# Revit family: EVAN WBT
name_source: partatom
category: Оборудование
units: mm (PartAtom-declared; Revit-internal decimal feet)

## family parameters
Всегда вертикально = Да
Классификация = Нет
На основе рабочей плоскости = Нет
Общий = Нет
При загрузке вырезать с полостями = Нет
Размер круглого соединителя = Использовать диаметр
Тип детали = Нормальный
Точка расчета площади = Нет

## types (14) — shared parameters
ADSK_Классификация нагрузок = Прочее
ADSK_Количество фаз = 1
ADSK_Коэффициент мощности = 1
ADSK_Материал = Конструкционная сталь с эмалевым покрытием
ADSK_Напряжение = 0 В
ADSK_Номинальная мощность = 0 Вт
ADSK_Расход ГВ = 0.0 л/с
ADSK_Расход ХВ = 0.0 л/с
Dкороба = 20 мм
G1int = 30 мм
G2int = 24 мм
URL = https://www.evan.ru
База = Бойлер косвенного нагрева напольный
Высота 1 = 20 мм
Материал корпуса = Конструкционная сталь с эмалевым покрытием
Напряжение питания для ТЭНа, В = 0 В
Пластик прозрачный = Пластик_прозрачный
Пластик_красный = Пластик_красный
Пластик_синий = Пластик_синий
Пластмасса_черная = Пластмасса_черная
Серый = Серый
Стекло = Стекло
Частота тока для ТЭНа, Гц = 0 Гц
Электрическая мощность ТЭНа N, кВт2) = 0 Вт

## per-type parameters (varying)
| type | ADSK_Полная мощность | D2_colp | DN1 | DN2 | Dбойлера | G1ext | G2ext | H3 | H5 | H7 | Диаметр1 | Диаметр2 | Объем, л |
| EVAN WBT 100 л. с одним змеевиком | 17 кВт | 27 мм | 25 мм | 20 мм | 490 мм | 31 мм | 26 мм | 554 мм | 854 мм | 734 мм | 236 мм | 239 мм | 104 |
| EVAN WBT 160 л. с одним змеевиком | 24 кВт | 27 мм | 25 мм | 20 мм | 590 мм | 31 мм | 26 мм | 542 мм | 857 мм | 707 мм | 286 мм | 289 мм | 173 |
| EVAN WBT 200 л. с одним змеевиком | 27 кВт | 27 мм | 25 мм | 20 мм | 590 мм | 31 мм | 26 мм | 679 мм | 1074 мм | 864 мм | 286 мм | 289 мм | 208 |
| EVAN WBT 300 л. с одним змеевиком | 36 кВт | 33 мм | 25 мм | 25 мм | 590 мм | 31 мм | 31 мм | 738 мм | 1613 мм | 913 мм | 286 мм | 289 мм | 284 |
| EVAN WBT 400 л. с одним змеевиком | 43 кВт | 33 мм | 25 мм | 25 мм | 750 мм | 31 мм | 31 мм | 698 мм | 1143 мм | 893 мм | 366 мм | 369 мм | 409 |
| EVAN WBT 500 л. с одним змеевиком | 53 кВт | 33 мм | 25 мм | 25 мм | 750 мм | 31 мм | 31 мм | 761 мм | 1386 мм | 986 мм | 366 мм | 369 мм | 510 |
| EVAN WBT 800 л. с одним змеевиком | 69 кВт | 40 мм | 32 мм | 32 мм | 950 мм | 38 мм | 38 мм | 843 мм | 1368 мм | 1063 мм | 466 мм | 469 мм | 814 |
| EVAN WBT 1000 л. с одним змеевиком | 82 кВт | 40 мм | 32 мм | 32 мм | 950 мм | 38 мм | 38 мм | 923 мм | 1698 мм | 1143 мм | 466 мм | 469 мм | 1004 |
| EVAN WBT 1500 л. с одним змеевиком | 108 кВт | 40 мм | 32 мм | 32 мм | 1060 мм | 38 мм | 38 мм | 1002 мм | 1957 мм | 1252 мм | 521 мм | 524 мм | 1463 |
| EVAN WBT 2000 л. с одним змеевиком | 126 кВт | 40 мм | 32 мм | 32 мм | 1200 мм | 38 мм | 38 мм | 997 мм | 1952 мм | 1217 мм | 591 мм | 594 мм | 1811 |
| EVAN WBT 2500 л. с одним змеевиком | 148 кВт | 48 мм | 32 мм | 40 мм | 1450 мм | 38 мм | 46 мм | 1104 мм | 1809 мм | 1344 мм | 716 мм | 719 мм | 2325 |
| EVAN WBT 3000 л. с одним змеевиком | 182 кВт | 48 мм | 32 мм | 40 мм | 1450 мм | 38 мм | 46 мм | 1264 мм | 2303 мм | 1504 мм | 716 мм | 719 мм | 2785 |
| EVAN WBT 4000 л. с одним змеевиком | 218 кВт | 48 мм | 50 мм | 40 мм | 1710 мм | 56 мм | 46 мм | 1288 мм | 2046 мм | 1528 мм | 846 мм | 849 мм | 4000 |
| EVAN WBT 5000 л. с одним змеевиком | 258 кВт | 48 мм | 50 мм | 40 мм | 1710 мм | 56 мм | 46 мм | 1508 мм | 2529 мм | 1744 мм | 846 мм | 849 мм | 5000 |
